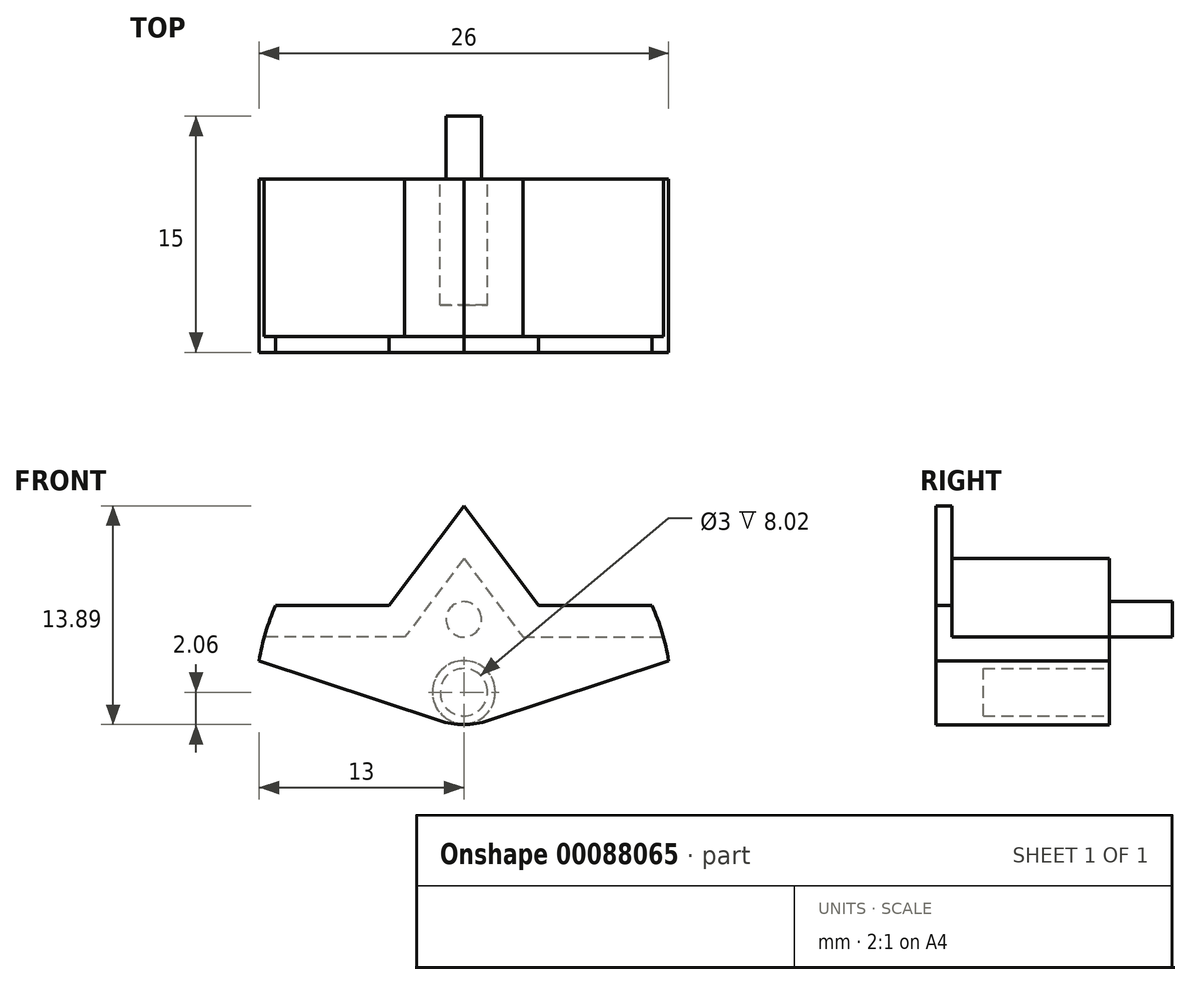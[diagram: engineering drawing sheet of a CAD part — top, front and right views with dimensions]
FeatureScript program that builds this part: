
annotation { "Feature Type Name" : "Feature", "Feature Type Description" : "" }
export const myFeature = defineFeature(function(context is Context, id is Id, definition is map)
    precondition{}
    {
        {
            var Q0;
            Q0=qCreatedBy(makeId("Front.planeOp"),FACE);
            var sketch = newSketch(context, id + "F0", { "sketchPlane" : qUnion([Q0])});
            skArc(sketch, "E0", {"start": v(-12.68, 3.5) * mm, "mid": v(-12.86, 2.75) * mm, "end": v(-13, 2) * mm});
            skPoint(sketch, "E1", {"position": v(0, 3.5) * mm});
            skLineSegment(sketch, "E2", {"start": v(0, 8.5) * mm, "end": v(-3.75, 3.5) * mm});
            skLineSegment(sketch, "E3", {"start": v(-3.75, 3.5) * mm, "end": v(-12.68, 3.5) * mm});
            skLineSegment(sketch, "E4", {"start": v(-13, 2) * mm, "end": v(-1.58, -1.8) * mm});
            skLineSegment(sketch, "E5", {"start": v(-1, -2) * mm, "end": v(0, -2) * mm, "construction": true});
            skLineSegment(sketch, "E6.MirrorCS", {"start": v(0, 8.5) * mm, "end": v(3.75, 3.5) * mm});
            skLineSegment(sketch, "E7.MirrorCS", {"start": v(3.75, 3.5) * mm, "end": v(12.68, 3.5) * mm});
            skLineSegment(sketch, "E8.MirrorCS", {"start": v(13, 2) * mm, "end": v(1.58, -1.8) * mm});
            skLineSegment(sketch, "E9.MirrorCS", {"start": v(1, -2) * mm, "end": v(0, -2) * mm, "construction": true});
            skArc(sketch, "E10.trimOffspring", {"start": v(13, 2) * mm, "mid": v(12.86, 2.75) * mm, "end": v(12.68, 3.5) * mm});
            skCircle(sketch, "E11", {"center": v(0, 0) * mm, "radius": 1.5 * mm});
            skPoint(sketch, "E12.orphan", {"position": v(1, -2) * mm});
            skPoint(sketch, "E13.visualSharp", {"position": v(0, -2.33) * mm});
            skArc(sketch, "E13.filletArc", {"start": v(-1.58, -1.8) * mm, "mid": v(0, -2.06) * mm, "end": v(1.58, -1.8) * mm});
            skSolve(sketch);
        }
        {
            var Q0;
            Q0=makeQuery(id+"F0.imprint","IMPRINT",FACE,{"disambiguationData":[TD([[makeQuery(id+"F0.imprint","IMPRINT",EDGE,{"derivedFrom":sQuery(id+"F0.wireOp",EDGE,"E0")}),1.0]])]});
            extrude(context, id + "F1", {"entities" : qUnion([Q0]), "depth" : 10 * mm});
        }
        {
            var Q0;
            Q0=makeQuery(id+"F1.opExtrude","CAP_FACE",FACE,{"disambiguationData":[OSD([sQuery(id+"F0.wireOp",EDGE,"E0"),sQuery(id+"F0.wireOp",EDGE,"E2"),sQuery(id+"F0.wireOp",EDGE,"E3"),sQuery(id+"F0.wireOp",EDGE,"E4"),sQuery(id+"F0.wireOp",EDGE,"E5"),sQuery(id+"F0.wireOp",EDGE,"E6.MirrorCS"),sQuery(id+"F0.wireOp",EDGE,"E7.MirrorCS"),sQuery(id+"F0.wireOp",EDGE,"E8.MirrorCS"),sQuery(id+"F0.wireOp",EDGE,"E9.MirrorCS"),sQuery(id+"F0.wireOp",EDGE,"E10.trimOffspring"),sQuery(id+"F0.wireOp",EDGE,"E11")])],"isStart":false});
            var sketch = newSketch(context, id + "F2", { "sketchPlane" : qUnion([Q0])});
            skCircle(sketch, "E14", {"center": v(0, 0) * mm, "radius": 2.75 * mm});
            skSolve(sketch);
        }
        {
            var Q0;
            Q0=makeQuery(id+"F1.opExtrude","CAP_FACE",FACE,{"disambiguationData":[OSD([sQuery(id+"F0.wireOp",EDGE,"E0"),sQuery(id+"F0.wireOp",EDGE,"E2"),sQuery(id+"F0.wireOp",EDGE,"E3"),sQuery(id+"F0.wireOp",EDGE,"E4"),sQuery(id+"F0.wireOp",EDGE,"E5"),sQuery(id+"F0.wireOp",EDGE,"E6.MirrorCS"),sQuery(id+"F0.wireOp",EDGE,"E7.MirrorCS"),sQuery(id+"F0.wireOp",EDGE,"E8.MirrorCS"),sQuery(id+"F0.wireOp",EDGE,"E9.MirrorCS"),sQuery(id+"F0.wireOp",EDGE,"E10.trimOffspring"),sQuery(id+"F0.wireOp",EDGE,"E11")])],"isStart":true});
            var sketch = newSketch(context, id + "F3", { "sketchPlane" : qUnion([Q0])});
            skPoint(sketch, "E15.0", {"position": v(0, 3.5) * mm});
            skCircle(sketch, "E16", {"center": v(0, 4.63) * mm, "radius": 1.13 * mm});
            skLineSegment(sketch, "E17", {"start": v(0, 8.5) * mm, "end": v(0, 0) * mm});
            skSolve(sketch);
        }
        {
            var Q0;
            {var subQ0=sQuery(id+"F3.wireOp",EDGE,"E17");var subQ1=sQuery(id+"F3.wireOp",EDGE,"E16");var subQ2=makeQuery(id+"F3.imprint","INTERSECT",VERTEX,{"disambiguationData":[OD(0.0)],"derivedFrom":[subQ1,subQ0]});Q0=makeQuery(id+"F3.imprint","IMPRINT",FACE,{"disambiguationData":[TD([[makeQuery(id+"F3.imprint","IMPRINT",EDGE,{"disambiguationData":[TD([[subQ2,1.0]])],"derivedFrom":subQ1}),1.0]])]});}
            var Q1;
            {var subQ0=sQuery(id+"F3.wireOp",EDGE,"E17");var subQ1=sQuery(id+"F3.wireOp",EDGE,"E16");var subQ2=makeQuery(id+"F3.imprint","INTERSECT",VERTEX,{"disambiguationData":[OD(0.0)],"derivedFrom":[subQ1,subQ0]});Q1=makeQuery(id+"F3.imprint","IMPRINT",FACE,{"disambiguationData":[TD([[makeQuery(id+"F3.imprint","IMPRINT",EDGE,{"disambiguationData":[TD([[subQ2,-1.0]])],"derivedFrom":subQ1}),1.0]])]});}
            extrude(context, id + "F4", {"entities" : qUnion([Q0, Q1]), "operationType" : NewBodyOperationType.ADD, "depth" : 4 * mm});
        }
        {
            var Q0;
            Q0=makeQuery(id+"F2.imprint","IMPRINT",FACE,{"disambiguationData":[TD([[makeQuery(id+"F2.imprint","IMPRINT",EDGE,{"derivedFrom":makeQuery(id+"F1.opExtrude","CAP_EDGE",EDGE,{"disambiguationData":[OSD([sQuery(id+"F0.wireOp",EDGE,"E11")])],"isStart":false})}),1.0]])]});
            extrude(context, id + "F5", {"entities" : qUnion([Q0]), "operationType" : NewBodyOperationType.ADD, "oppositeDirection" : true, "depth" : 2 * mm});
        }
        {
            var Q0;
            Q0=makeQuery(id+"F1.opExtrude","CAP_FACE",FACE,{"disambiguationData":[OSD([sQuery(id+"F0.wireOp",EDGE,"E0"),sQuery(id+"F0.wireOp",EDGE,"E2"),sQuery(id+"F0.wireOp",EDGE,"E3"),sQuery(id+"F0.wireOp",EDGE,"E4"),sQuery(id+"F0.wireOp",EDGE,"E5"),sQuery(id+"F0.wireOp",EDGE,"E6.MirrorCS"),sQuery(id+"F0.wireOp",EDGE,"E7.MirrorCS"),sQuery(id+"F0.wireOp",EDGE,"E8.MirrorCS"),sQuery(id+"F0.wireOp",EDGE,"E9.MirrorCS"),sQuery(id+"F0.wireOp",EDGE,"E10.trimOffspring"),sQuery(id+"F0.wireOp",EDGE,"E11")])],"isStart":true});
            var sketch = newSketch(context, id + "F6", { "sketchPlane" : qUnion([Q0])});
            skCircle(sketch, "E18", {"center": v(0, 0) * mm, "radius": 2 * mm});
            skLineSegment(sketch, "E19.0", {"start": v(2.5, -2) * mm, "end": v(-2.5, -2) * mm});
            skSolve(sketch);
        }
        {
            var Q0;
            Q0=makeQuery(id+"F6.imprint","IMPRINT",FACE,{"disambiguationData":[TD([[makeQuery(id+"F6.imprint","IMPRINT",EDGE,{"derivedFrom":sQuery(id+"F6.wireOp",EDGE,"E18")}),1.0]])]});
            extrude(context, id + "F7", {"entities" : qUnion([Q0]), "operationType" : NewBodyOperationType.ADD, "depth" : 0.02 * mm});
        }
        {
            var Q0;
            {var subQ0=sQuery(id+"F0.wireOp",EDGE,"E11");Q0=makeQuery(id+"F5.boolean.opBoolean","MERGE",FACE,{"derivedFrom":[makeQuery(id+"F1.opExtrude","CAP_FACE",FACE,{"disambiguationData":[OSD([sQuery(id+"F0.wireOp",EDGE,"E0"),sQuery(id+"F0.wireOp",EDGE,"E2"),sQuery(id+"F0.wireOp",EDGE,"E3"),sQuery(id+"F0.wireOp",EDGE,"E4"),sQuery(id+"F0.wireOp",EDGE,"E6.MirrorCS"),sQuery(id+"F0.wireOp",EDGE,"E7.MirrorCS"),sQuery(id+"F0.wireOp",EDGE,"E8.MirrorCS"),sQuery(id+"F0.wireOp",EDGE,"E10.trimOffspring"),subQ0,sQuery(id+"F0.wireOp",EDGE,"E13.filletArc")])],"isStart":false}),makeQuery(id+"F5.opExtrude","CAP_FACE",FACE,{"disambiguationData":[OSD([subQ0])],"isStart":true})]});}
            var sketch = newSketch(context, id + "F8", { "sketchPlane" : qUnion([Q0])});
            skLineSegment(sketch, "E20.0", {"start": v(-4.75, 5.5) * mm, "end": v(-12.36, 5.5) * mm});
            skLineSegment(sketch, "E20.1", {"start": v(0, 11.83) * mm, "end": v(-4.75, 5.5) * mm});
            skLineSegment(sketch, "E20.2", {"start": v(0, 11.83) * mm, "end": v(4.75, 5.5) * mm});
            skLineSegment(sketch, "E20.3", {"start": v(4.75, 5.5) * mm, "end": v(12.36, 5.5) * mm});
            skArc(sketch, "E21.0", {"start": v(-11.95, 5.5) * mm, "mid": v(-12.6, 3.79) * mm, "end": v(-13, 2) * mm});
            skLineSegment(sketch, "E22.0", {"start": v(-3.75, 3.5) * mm, "end": v(-12.68, 3.5) * mm});
            skLineSegment(sketch, "E23.0", {"start": v(0, 8.5) * mm, "end": v(-3.75, 3.5) * mm});
            skLineSegment(sketch, "E24.0", {"start": v(0, 8.5) * mm, "end": v(3.75, 3.5) * mm});
            skLineSegment(sketch, "E25.0", {"start": v(3.75, 3.5) * mm, "end": v(12.68, 3.5) * mm});
            skArc(sketch, "E26.0", {"start": v(13, 2) * mm, "mid": v(12.6, 3.79) * mm, "end": v(11.95, 5.5) * mm});
            skSolve(sketch);
        }
        {
            var Q0;
            {var subQ4=sQuery(id+"F8.wireOp",EDGE,"E20.1");Q0=makeQuery(id+"F8.imprint","IMPRINT",FACE,{"disambiguationData":[TD([[makeQuery(id+"F8.imprint","IMPRINT",EDGE,{"derivedFrom":subQ4}),1.0]])]});}
            var Q1;
            {var subQ0=sQuery(id+"F8.wireOp",EDGE,"E22.0");Q1=makeQuery(id+"F8.imprint","IMPRINT",FACE,{"disambiguationData":[TD([[makeQuery(id+"F8.imprint","IMPRINT",EDGE,{"derivedFrom":subQ0}),1.0]])]});}
            extrude(context, id + "F9", {"entities" : qUnion([Q0, Q1]), "operationType" : NewBodyOperationType.ADD, "depth" : 1 * mm});
        }
    });
